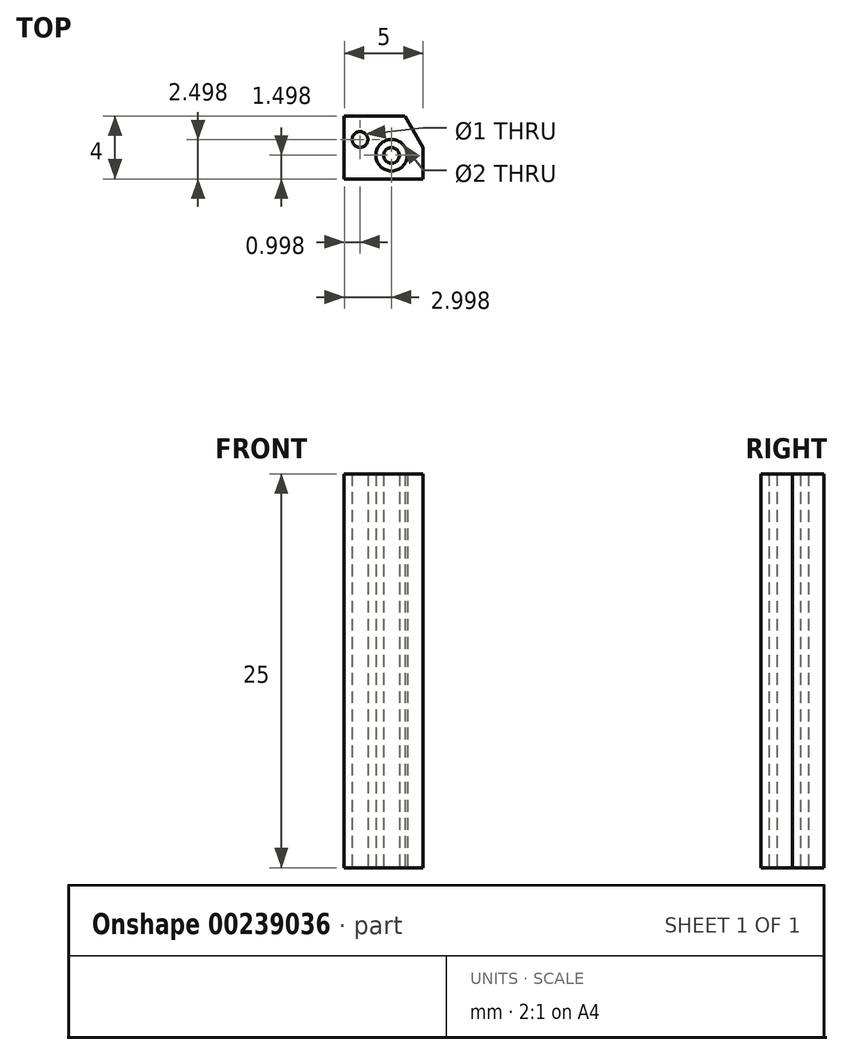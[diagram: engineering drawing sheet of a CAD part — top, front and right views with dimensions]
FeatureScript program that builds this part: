
annotation { "Feature Type Name" : "Feature", "Feature Type Description" : "" }
export const myFeature = defineFeature(function(context is Context, id is Id, definition is map)
    precondition{}
    {
        {
            var Q0;
            Q0=qCreatedBy(makeId("Top.planeOp"),FACE);
            var sketch = newSketch(context, id + "F0", { "sketchPlane" : qUnion([Q0])});
            skLineSegment(sketch, "E0", {"start": v(-50.24, -8.71) * mm, "end": v(-50.24, -6.21) * mm});
            skLineSegment(sketch, "E1", {"start": v(-50.24, -6.21) * mm, "end": v(-50.24, -4.71) * mm});
            skPoint(sketch, "E2", {"position": v(-49.24, -6.21) * mm});
            skCircle(sketch, "E3", {"center": v(-49.24, -6.21) * mm, "radius": 0.5 * mm});
            skLineSegment(sketch, "E4", {"start": v(-50.24, -8.71) * mm, "end": v(-47.24, -8.71) * mm});
            skLineSegment(sketch, "E5", {"start": v(-47.24, -8.71) * mm, "end": v(-45.24, -8.71) * mm});
            skPoint(sketch, "E6", {"position": v(-47.24, -7.21) * mm});
            skCircle(sketch, "E7", {"center": v(-47.24, -7.21) * mm, "radius": 1 * mm});
            skLineSegment(sketch, "E8", {"start": v(-45.24, -8.71) * mm, "end": v(-45.24, -6.71) * mm});
            skLineSegment(sketch, "E9", {"start": v(-45.24, -6.71) * mm, "end": v(-46.4, -4.71) * mm});
            skLineSegment(sketch, "E10", {"start": v(-50.24, -4.71) * mm, "end": v(-46.4, -4.71) * mm});
            skSolve(sketch);
        }
        {
            var Q0;
            Q0=qCreatedBy(makeId("Top.planeOp"),FACE);
            var sketch = newSketch(context, id + "F1", { "sketchPlane" : qUnion([Q0])});
            skCircle(sketch, "E11", {"center": v(-47.24, -7.22) * mm, "radius": 0.5 * mm});
            skSolve(sketch);
        }
        {
            var Q0;
            Q0=makeQuery(id+"F0.imprint","IMPRINT",FACE,{"disambiguationData":[TD([[makeQuery(id+"F0.imprint","IMPRINT",EDGE,{"derivedFrom":sQuery(id+"F0.wireOp",EDGE,"E0")}),-1.0]])]});
            extrude(context, id + "F2", {"entities" : qUnion([Q0]), "depth" : 25 * mm});
        }
        {
            var Q0;
            Q0=makeQuery(id+"F1.imprint","IMPRINT",FACE,{"disambiguationData":[TD([[makeQuery(id+"F1.imprint","IMPRINT",EDGE,{"derivedFrom":sQuery(id+"F1.wireOp",EDGE,"E11")}),1.0]])]});
            extrude(context, id + "F3", {"entities" : qUnion([Q0]), "depth" : 25 * mm});
        }
    });
